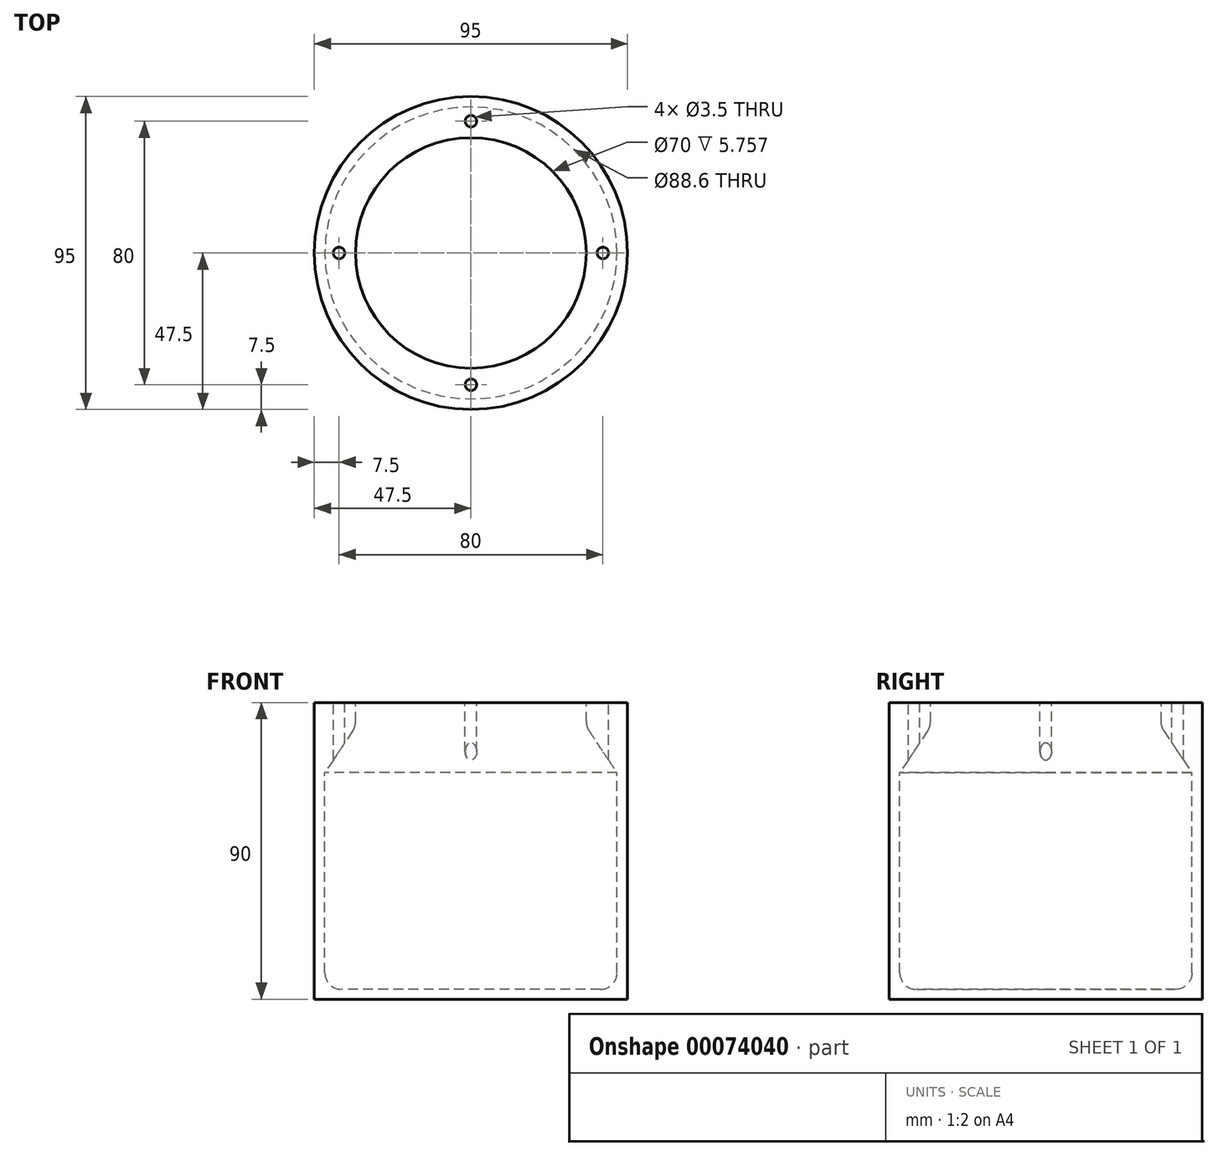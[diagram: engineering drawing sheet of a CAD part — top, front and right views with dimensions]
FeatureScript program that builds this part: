
annotation { "Feature Type Name" : "Feature", "Feature Type Description" : "" }
export const myFeature = defineFeature(function(context is Context, id is Id, definition is map)
    precondition{}
    {
        {
            var Q0;
            Q0=qCreatedBy(makeId("Front.planeOp"),FACE);
            var sketch = newSketch(context, id + "F0", { "sketchPlane" : qUnion([Q0])});
            skLineSegment(sketch, "E0", {"start": v(0, 0) * mm, "end": v(47.5, 0) * mm});
            skLineSegment(sketch, "E1", {"start": v(47.5, 0) * mm, "end": v(47.5, 90) * mm});
            skLineSegment(sketch, "E2", {"start": v(47.5, 90) * mm, "end": v(35, 90) * mm});
            skLineSegment(sketch, "E3", {"start": v(44.3, 68.75) * mm, "end": v(44.3, 8) * mm});
            skLineSegment(sketch, "E4", {"start": v(39.3, 3) * mm, "end": v(0, 3) * mm});
            skLineSegment(sketch, "E5", {"start": v(0, 3) * mm, "end": v(0, 0) * mm});
            skLineSegment(sketch, "E6", {"start": v(44.3, 68.75) * mm, "end": v(47.5, 68.75) * mm});
            skPoint(sketch, "E7.visualSharp", {"position": v(44.3, 3) * mm});
            skArc(sketch, "E7.filletArc", {"start": v(39.3, 3) * mm, "mid": v(42.84, 4.46) * mm, "end": v(44.3, 8) * mm});
            skPoint(sketch, "E8.visualSharp", {"position": v(47.5, 0) * mm});
            skLineSegment(sketch, "E8.filletArc", {"start": v(47.5, 0) * mm, "end": v(47.5, 0) * mm});
            skLineSegment(sketch, "E9", {"start": v(35, 90) * mm, "end": v(35, 84.24) * mm});
            skLineSegment(sketch, "E10", {"start": v(35.84, 81.47) * mm, "end": v(44.3, 68.75) * mm});
            skPoint(sketch, "E11.visualSharp", {"position": v(35, 82.73) * mm});
            skArc(sketch, "E11.filletArc", {"start": v(35, 84.24) * mm, "mid": v(35.21, 82.8) * mm, "end": v(35.84, 81.47) * mm});
            skSolve(sketch);
        }
        {
            var Q0;
            Q0=makeQuery(id+"F0.imprint","IMPRINT",FACE,{"disambiguationData":[TD([[makeQuery(id+"F0.imprint","IMPRINT",EDGE,{"derivedFrom":sQuery(id+"F0.wireOp",EDGE,"E0")}),1.0]])]});
            var Q1;
            {var subQ0=sQuery(id+"F0.wireOp",EDGE,"E2");Q1=makeQuery(id+"F0.imprint","IMPRINT",FACE,{"disambiguationData":[TD([[makeQuery(id+"F0.imprint","IMPRINT",EDGE,{"derivedFrom":subQ0}),1.0]])]});}
            var Q2;
            Q2=sQuery(id+"F0.wireOp",EDGE,"E5");
            revolve(context, id + "F1", {"entities" : qUnion([Q0, Q1]), "axis" : qUnion([Q2]), "revolveType" : RevolveType.FULL});
        }
        {
            var Q0;
            Q0=makeQuery(id+"F1.opRevolve","SWEPT_FACE",FACE,{"disambiguationData":[OSD([sQuery(id+"F0.wireOp",EDGE,"E2")])]});
            var sketch = newSketch(context, id + "F2", { "sketchPlane" : qUnion([Q0])});
            skCircle(sketch, "E12", {"center": v(0, 40) * mm, "radius": 1.75 * mm});
            skCircle(sketch, "E13", {"center": v(40, 0) * mm, "radius": 1.75 * mm});
            skCircle(sketch, "E14", {"center": v(-40, 0) * mm, "radius": 1.75 * mm});
            skCircle(sketch, "E15", {"center": v(0, -40) * mm, "radius": 1.75 * mm});
            skLineSegment(sketch, "E16", {"start": v(0, 0) * mm, "end": v(0, 40) * mm});
            skLineSegment(sketch, "E17", {"start": v(0, 0) * mm, "end": v(40, 0) * mm});
            skLineSegment(sketch, "E18", {"start": v(0, 0) * mm, "end": v(0, -40) * mm});
            skLineSegment(sketch, "E19", {"start": v(0, 0) * mm, "end": v(-40, 0) * mm});
            skSolve(sketch);
        }
        {
            var Q0;
            Q0=makeQuery(id+"F2.imprint","IMPRINT",FACE,{"disambiguationData":[TD([[makeQuery(id+"F2.imprint","IMPRINT",EDGE,{"derivedFrom":sQuery(id+"F2.wireOp",EDGE,"E12")}),1.0]])]});
            var Q1;
            Q1=makeQuery(id+"F2.imprint","IMPRINT",FACE,{"disambiguationData":[TD([[makeQuery(id+"F2.imprint","IMPRINT",EDGE,{"derivedFrom":sQuery(id+"F2.wireOp",EDGE,"E13")}),1.0]])]});
            var Q2;
            Q2=makeQuery(id+"F2.imprint","IMPRINT",FACE,{"disambiguationData":[TD([[makeQuery(id+"F2.imprint","IMPRINT",EDGE,{"derivedFrom":sQuery(id+"F2.wireOp",EDGE,"E15")}),1.0]])]});
            var Q3;
            Q3=makeQuery(id+"F2.imprint","IMPRINT",FACE,{"disambiguationData":[TD([[makeQuery(id+"F2.imprint","IMPRINT",EDGE,{"derivedFrom":sQuery(id+"F2.wireOp",EDGE,"E14")}),1.0]])]});
            var Q4;
            Q4=sQuery(id+"F2.wireOp",EDGE,"E12");
            var Q5;
            Q5=sQuery(id+"F2.wireOp",EDGE,"E13");
            var Q6;
            Q6=sQuery(id+"F2.wireOp",EDGE,"E15");
            var Q7;
            Q7=sQuery(id+"F2.wireOp",EDGE,"E14");
            extrude(context, id + "F3", {"entities" : qUnion([Q0, Q1, Q2, Q3]), "operationType" : NewBodyOperationType.REMOVE, "surfaceEntities" : qUnion([Q4, Q5, Q6, Q7]), "oppositeDirection" : true, "depth" : 25 * mm});
        }
    });
